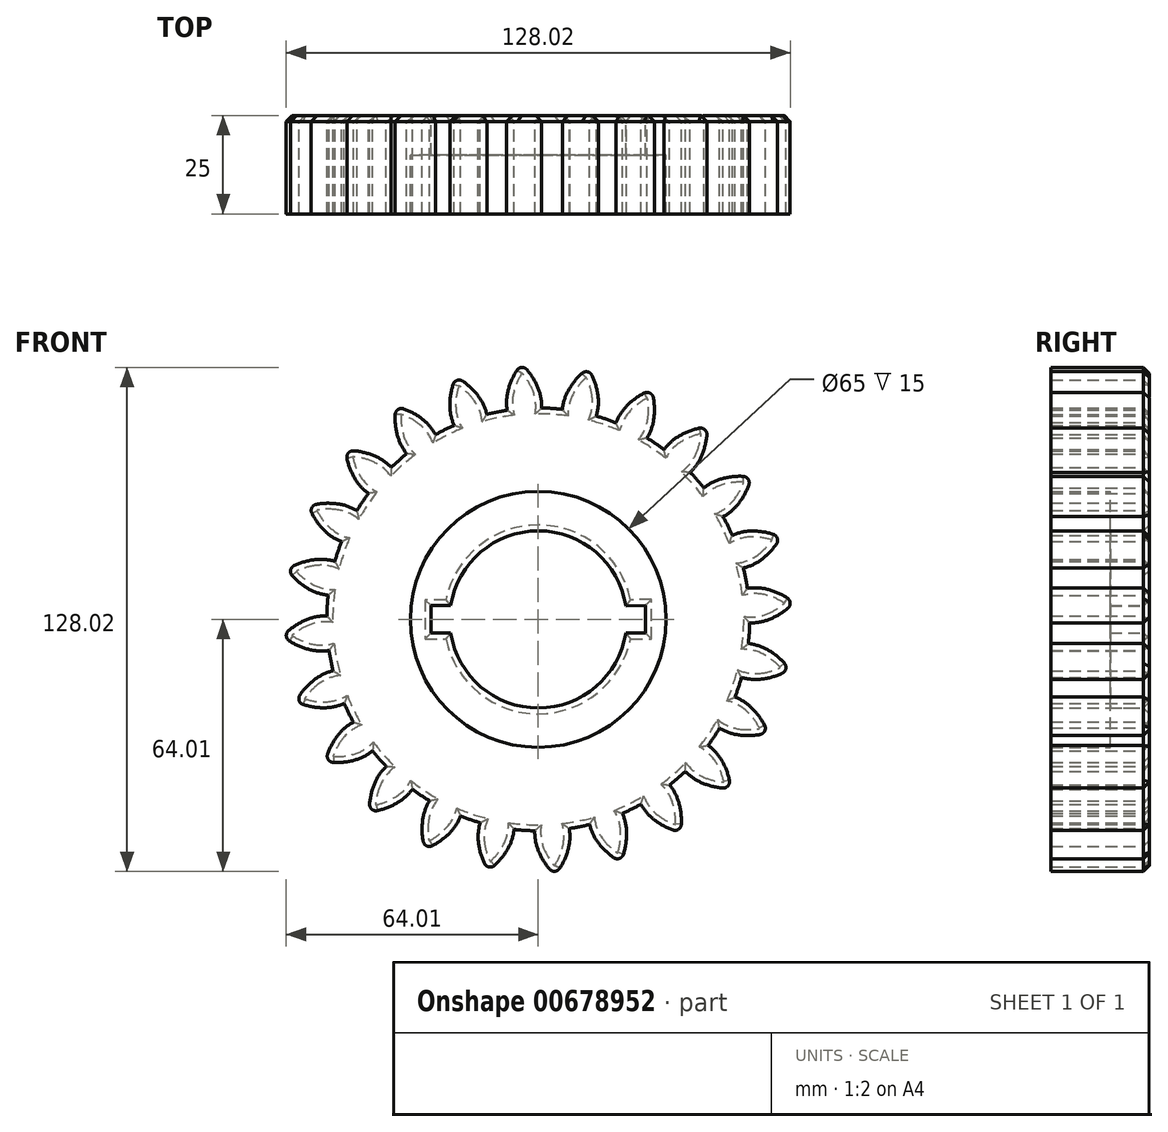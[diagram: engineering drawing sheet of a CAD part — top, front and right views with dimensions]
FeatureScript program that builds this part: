
annotation { "Feature Type Name" : "Feature", "Feature Type Description" : "" }
export const myFeature = defineFeature(function(context is Context, id is Id, definition is map)
    precondition{}
    {
        {
            var Q0;
            Q0=qCreatedBy(makeId("Front.planeOp"),FACE);
            var sketch = newSketch(context, id + "F0", { "sketchPlane" : qUnion([Q0])});
            skCircle(sketch, "E0", {"center": v(0, 0) * mm, "radius": 53.72 * mm});
            skCircle(sketch, "E1", {"center": v(0, 0) * mm, "radius": 58.67 * mm, "construction": true});
            skCircle(sketch, "E2", {"center": v(0, 0) * mm, "radius": 63.5 * mm, "construction": true});
            skLineSegment(sketch, "E3", {"start": v(0, 0) * mm, "end": v(0, 76.88) * mm, "construction": true});
            skLineSegment(sketch, "E4", {"start": v(0, 0) * mm, "end": v(-5.13, 78.22) * mm, "construction": true});
            skLineSegment(sketch, "E5", {"start": v(0, 58.67) * mm, "end": v(-76.8, 58.67) * mm, "construction": true});
            skLineSegment(sketch, "E6", {"start": v(0, 58.67) * mm, "end": v(-72.34, 32.34) * mm, "construction": true});
            skCircle(sketch, "E7", {"center": v(0, 58.67) * mm, "radius": 14.6 * mm, "construction": true});
            skCircle(sketch, "E8", {"center": v(0, 0) * mm, "radius": 55.14 * mm, "construction": true});
            skCircle(sketch, "E9", {"center": v(-13.72, 53.68) * mm, "radius": 14.6 * mm, "construction": true});
            skArc(sketch, "E10", {"start": v(0, 58.67) * mm, "mid": v(-1.24, 61.17) * mm, "end": v(-2.86, 63.44) * mm});
            skArc(sketch, "E11", {"start": v(0.88, 53.71) * mm, "mid": v(0.7, 56.24) * mm, "end": v(0, 58.67) * mm});
            skArc(sketch, "E12.MirrorCS", {"start": v(-7.66, 58.17) * mm, "mid": v(-6.76, 60.8) * mm, "end": v(-5.45, 63.27) * mm});
            skArc(sketch, "E13.MirrorCS", {"start": v(-7.88, 53.14) * mm, "mid": v(-8.03, 55.67) * mm, "end": v(-7.66, 58.17) * mm});
            skArc(sketch, "E14", {"start": v(-2.86, 63.44) * mm, "mid": v(-4.2, 64) * mm, "end": v(-5.45, 63.27) * mm});
            skArc(sketch, "E15.1.0", {"start": v(-46.55, -35.72) * mm, "mid": v(-49.28, -36.26) * mm, "end": v(-52.07, -36.35) * mm});
            skArc(sketch, "E15.1.1", {"start": v(-42.08, -33.4) * mm, "mid": v(-44.2, -34.79) * mm, "end": v(-46.55, -35.72) * mm});
            skArc(sketch, "E15.1.2", {"start": v(-53.5, -34.2) * mm, "mid": v(-53.33, -35.64) * mm, "end": v(-52.07, -36.35) * mm});
            skArc(sketch, "E15.1.3", {"start": v(-50.81, -29.34) * mm, "mid": v(-52.36, -31.66) * mm, "end": v(-53.5, -34.2) * mm});
            skArc(sketch, "E15.1.4", {"start": v(-46.96, -26.1) * mm, "mid": v(-49.05, -27.52) * mm, "end": v(-50.81, -29.34) * mm});
            skArc(sketch, "E15.2.0", {"start": v(54.2, -22.45) * mm, "mid": v(56.04, -24.55) * mm, "end": v(57.51, -26.91) * mm});
            skArc(sketch, "E15.2.1", {"start": v(49.96, -19.74) * mm, "mid": v(52.22, -20.88) * mm, "end": v(54.2, -22.45) * mm});
            skArc(sketch, "E15.2.2", {"start": v(56.37, -29.24) * mm, "mid": v(57.53, -28.37) * mm, "end": v(57.51, -26.91) * mm});
            skArc(sketch, "E15.2.3", {"start": v(50.81, -29.34) * mm, "mid": v(53.6, -29.51) * mm, "end": v(56.37, -29.24) * mm});
            skArc(sketch, "E15.2.4", {"start": v(46.08, -27.62) * mm, "mid": v(48.36, -28.72) * mm, "end": v(50.81, -29.34) * mm});
            skCircle(sketch, "E16", {"center": v(0, 0) * mm, "radius": 32.5 * mm});
            skCircle(sketch, "E17", {"center": v(0, 0) * mm, "radius": 22.5 * mm});
            skLineSegment(sketch, "E18", {"start": v(-22.23, 3.5) * mm, "end": v(-27.23, 3.5) * mm});
            skLineSegment(sketch, "E19", {"start": v(-27.23, 3.5) * mm, "end": v(-27.23, -3.5) * mm});
            skLineSegment(sketch, "E20", {"start": v(-27.23, -3.5) * mm, "end": v(-22.23, -3.5) * mm});
            skLineSegment(sketch, "E21", {"start": v(22.24, -3.44) * mm, "end": v(27.24, -3.44) * mm});
            skLineSegment(sketch, "E22", {"start": v(27.24, -3.44) * mm, "end": v(27.24, 3.56) * mm});
            skLineSegment(sketch, "E23", {"start": v(27.24, 3.56) * mm, "end": v(22.24, 3.43) * mm});
            skSolve(sketch);
        }
        {
            var Q0;
            {var subQ0=sQuery(id+"F0.wireOp",EDGE,"E0");var subQ1=makeQuery(id+"F0.imprint","INTERSECT",VERTEX,{"derivedFrom":[subQ0,sQuery(id+"F0.wireOp",EDGE,"E11")]});Q0=makeQuery(id+"F0.imprint","IMPRINT",FACE,{"disambiguationData":[TD([[makeQuery(id+"F0.imprint","IMPRINT",EDGE,{"disambiguationData":[TD([[subQ1,-1.0]])],"derivedFrom":subQ0}),1.0]])]});}
            var Q1;
            Q1=makeQuery(id+"F0.imprint","IMPRINT",FACE,{"disambiguationData":[TD([[makeQuery(id+"F0.imprint","IMPRINT",EDGE,{"derivedFrom":sQuery(id+"F0.wireOp",EDGE,"E10")}),1.0]])]});
            extrude(context, id + "F1", {"entities" : qUnion([Q0, Q1]), "depth" : 25 * mm, "offsetDistance" : 25 * mm});
        }
        {
            var Q0;
            Q0=makeQuery(id+"F1.opExtrude","SWEPT_BODY",BODY,{"disambiguationData":[OSD([sQuery(id+"F0.wireOp",EDGE,"E0"),sQuery(id+"F0.wireOp",EDGE,"E10"),sQuery(id+"F0.wireOp",EDGE,"E11"),sQuery(id+"F0.wireOp",EDGE,"E12.MirrorCS"),sQuery(id+"F0.wireOp",EDGE,"E13.MirrorCS"),sQuery(id+"F0.wireOp",EDGE,"E14")])]});
            var Q1;
            Q1=makeQuery(id+"F1.opExtrude","SWEPT_FACE",FACE,{"disambiguationData":[OSD([sQuery(id+"F0.wireOp",EDGE,"E0")])]});
            circularPattern(context, id + "F2", {"entities" : qUnion([Q0]), "axis" : qUnion([Q1]), "angle" : 360 * degree, "instanceCount" : 24, "equalSpace" : true});
        }
        {
            var Q0;
            Q0=makeQuery(id+"F0.imprint","IMPRINT",FACE,{"disambiguationData":[TD([[makeQuery(id+"F0.imprint","IMPRINT",EDGE,{"derivedFrom":sQuery(id+"F0.wireOp",EDGE,"E16")}),1.0]])]});
            extrude(context, id + "F3", {"entities" : qUnion([Q0]), "operationType" : NewBodyOperationType.ADD, "depth" : 10 * mm, "offsetDistance" : 25 * mm});
        }
        {
            var Q0;
            {var subQ0=sQuery(id+"F0.wireOp",EDGE,"E16");var subQ1=makeQuery(id+"F1.opExtrude","CAP_FACE",FACE,{"disambiguationData":[OSD([sQuery(id+"F0.wireOp",EDGE,"E0"),sQuery(id+"F0.wireOp",EDGE,"E10"),sQuery(id+"F0.wireOp",EDGE,"E11"),sQuery(id+"F0.wireOp",EDGE,"E12.MirrorCS"),sQuery(id+"F0.wireOp",EDGE,"E13.MirrorCS"),sQuery(id+"F0.wireOp",EDGE,"E14"),subQ0])],"isStart":true});Q0=makeQuery(id+"F3.boolean.opBoolean","MERGE",FACE,{"derivedFrom":[subQ1,makeQuery(id+"F2.opPattern","COPY",FACE,{"derivedFrom":subQ1,"instanceName":"1"}),makeQuery(id+"F2.opPattern","COPY",FACE,{"derivedFrom":subQ1,"instanceName":"2"}),makeQuery(id+"F2.opPattern","COPY",FACE,{"derivedFrom":subQ1,"instanceName":"3"}),makeQuery(id+"F2.opPattern","COPY",FACE,{"derivedFrom":subQ1,"instanceName":"4"}),makeQuery(id+"F2.opPattern","COPY",FACE,{"derivedFrom":subQ1,"instanceName":"5"}),makeQuery(id+"F2.opPattern","COPY",FACE,{"derivedFrom":subQ1,"instanceName":"6"}),makeQuery(id+"F2.opPattern","COPY",FACE,{"derivedFrom":subQ1,"instanceName":"7"}),makeQuery(id+"F2.opPattern","COPY",FACE,{"derivedFrom":subQ1,"instanceName":"8"}),makeQuery(id+"F2.opPattern","COPY",FACE,{"derivedFrom":subQ1,"instanceName":"9"}),makeQuery(id+"F2.opPattern","COPY",FACE,{"derivedFrom":subQ1,"instanceName":"10"}),makeQuery(id+"F2.opPattern","COPY",FACE,{"derivedFrom":subQ1,"instanceName":"11"}),makeQuery(id+"F2.opPattern","COPY",FACE,{"derivedFrom":subQ1,"instanceName":"12"}),makeQuery(id+"F2.opPattern","COPY",FACE,{"derivedFrom":subQ1,"instanceName":"13"}),makeQuery(id+"F2.opPattern","COPY",FACE,{"derivedFrom":subQ1,"instanceName":"14"}),makeQuery(id+"F2.opPattern","COPY",FACE,{"derivedFrom":subQ1,"instanceName":"15"}),makeQuery(id+"F2.opPattern","COPY",FACE,{"derivedFrom":subQ1,"instanceName":"16"}),makeQuery(id+"F2.opPattern","COPY",FACE,{"derivedFrom":subQ1,"instanceName":"17"}),makeQuery(id+"F2.opPattern","COPY",FACE,{"derivedFrom":subQ1,"instanceName":"18"}),makeQuery(id+"F2.opPattern","COPY",FACE,{"derivedFrom":subQ1,"instanceName":"19"}),makeQuery(id+"F2.opPattern","COPY",FACE,{"derivedFrom":subQ1,"instanceName":"20"}),makeQuery(id+"F2.opPattern","COPY",FACE,{"derivedFrom":subQ1,"instanceName":"21"}),makeQuery(id+"F2.opPattern","COPY",FACE,{"derivedFrom":subQ1,"instanceName":"22"}),makeQuery(id+"F2.opPattern","COPY",FACE,{"derivedFrom":subQ1,"instanceName":"23"}),makeQuery(id+"F3.opExtrude","CAP_FACE",FACE,{"disambiguationData":[OSD([subQ0,sQuery(id+"F0.wireOp",EDGE,"E17"),sQuery(id+"F0.wireOp",EDGE,"E18"),sQuery(id+"F0.wireOp",EDGE,"E19"),sQuery(id+"F0.wireOp",EDGE,"E20"),sQuery(id+"F0.wireOp",EDGE,"E21"),sQuery(id+"F0.wireOp",EDGE,"E22"),sQuery(id+"F0.wireOp",EDGE,"E23")])],"isStart":true})]});}
            chamfer(context, id + "F4", {"entities" : qUnion([Q0]), "width" : 1.5 * mm, "tangentPropagation" : true});
        }
    });
